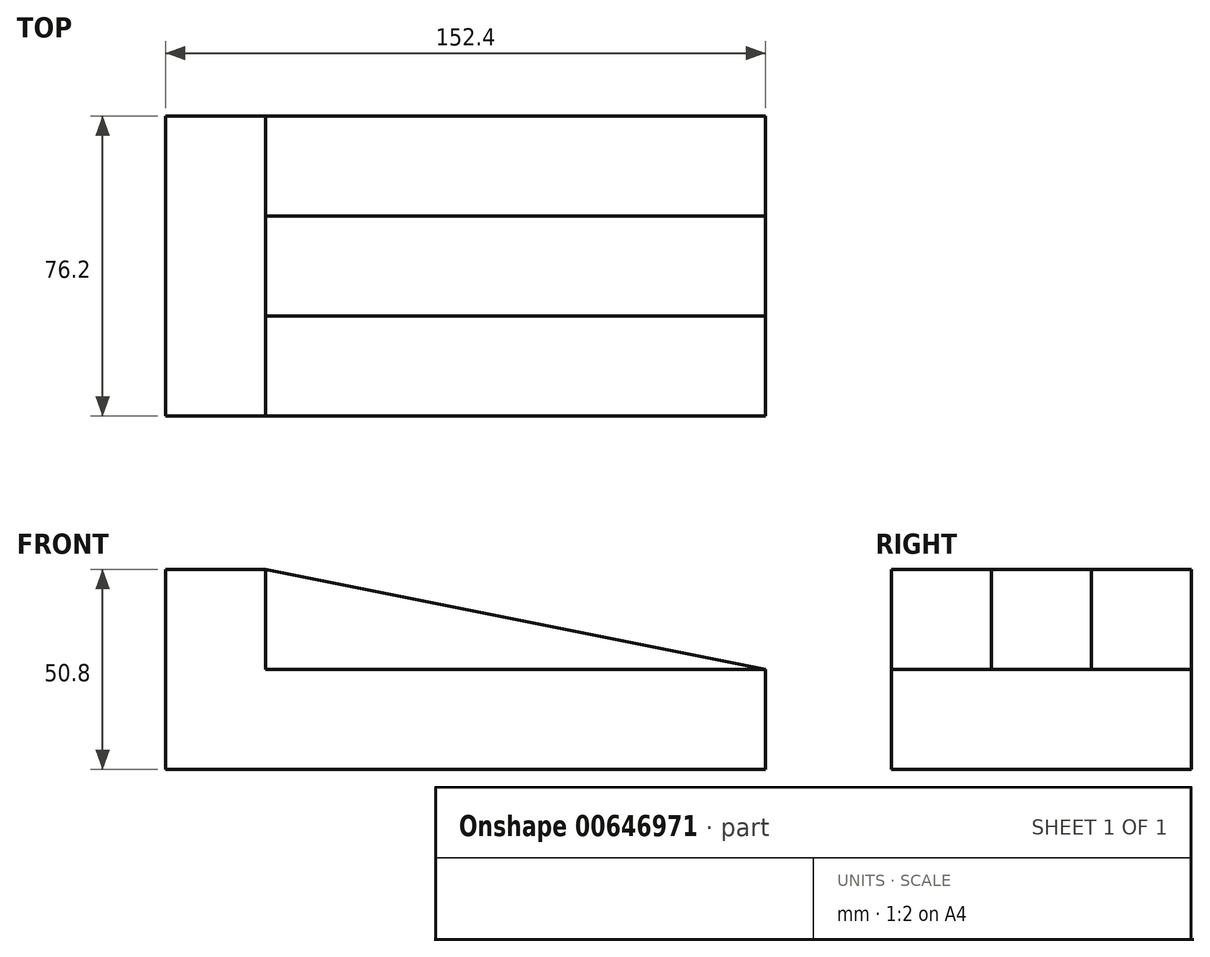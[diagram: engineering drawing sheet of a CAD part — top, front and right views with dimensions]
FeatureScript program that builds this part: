
annotation { "Feature Type Name" : "Feature", "Feature Type Description" : "" }
export const myFeature = defineFeature(function(context is Context, id is Id, definition is map)
    precondition{}
    {
        {
            var Q0;
            Q0=qCreatedBy(makeId("Front.planeOp"),FACE);
            var sketch = newSketch(context, id + "F0", { "sketchPlane" : qUnion([Q0])});
            skLineSegment(sketch, "E0", {"start": v(-65.92, 61.18) * mm, "end": v(-65.92, 10.38) * mm});
            skLineSegment(sketch, "E1", {"start": v(-65.92, 10.38) * mm, "end": v(86.48, 10.38) * mm});
            skLineSegment(sketch, "E2", {"start": v(86.48, 10.38) * mm, "end": v(86.48, 35.78) * mm});
            skLineSegment(sketch, "E3", {"start": v(86.48, 35.78) * mm, "end": v(-40.52, 35.78) * mm});
            skLineSegment(sketch, "E4", {"start": v(-40.52, 35.78) * mm, "end": v(-40.52, 61.18) * mm});
            skLineSegment(sketch, "E5", {"start": v(-40.52, 61.18) * mm, "end": v(-65.92, 61.18) * mm});
            skLineSegment(sketch, "E6", {"start": v(-40.52, 61.18) * mm, "end": v(86.48, 35.78) * mm});
            skSolve(sketch);
        }
        {
            var Q0;
            Q0=makeQuery(id+"F0.imprint","IMPRINT",FACE,{"disambiguationData":[TD([[makeQuery(id+"F0.imprint","IMPRINT",EDGE,{"derivedFrom":sQuery(id+"F0.wireOp",EDGE,"E0")}),1.0]])]});
            extrude(context, id + "F1", {"entities" : qUnion([Q0]), "depth" : 50.8 * mm, "offsetDistance" : 25.4 * mm, "hasSecondDirection" : true, "secondDirectionOppositeDirection" : true, "secondDirectionDepth" : 25.4 * mm});
        }
        {
            var Q0;
            Q0=makeQuery(id+"F0.imprint","IMPRINT",FACE,{"disambiguationData":[TD([[makeQuery(id+"F0.imprint","IMPRINT",EDGE,{"derivedFrom":sQuery(id+"F0.wireOp",EDGE,"E3")}),-1.0]])]});
            extrude(context, id + "F2", {"entities" : qUnion([Q0]), "operationType" : NewBodyOperationType.ADD, "depth" : 25.4 * mm, "offsetDistance" : 25.4 * mm});
        }
    });
